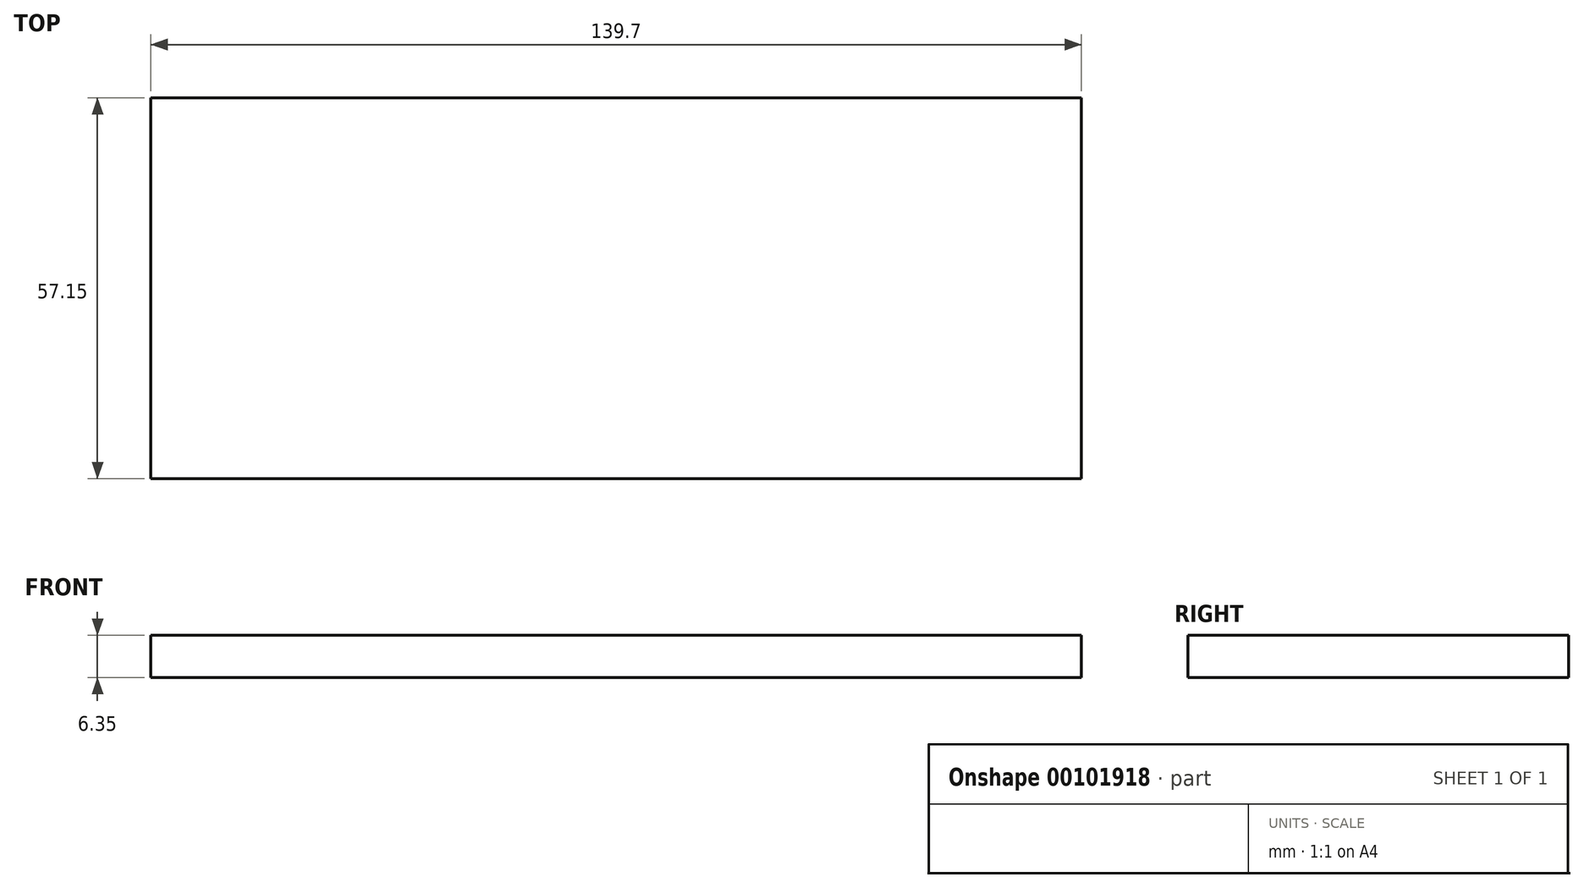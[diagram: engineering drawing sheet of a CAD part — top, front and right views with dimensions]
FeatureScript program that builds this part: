
annotation { "Feature Type Name" : "Feature", "Feature Type Description" : "" }
export const myFeature = defineFeature(function(context is Context, id is Id, definition is map)
    precondition{}
    {
        {
            var Q0;
            Q0=qCreatedBy(makeId("Top.planeOp"),FACE);
            var sketch = newSketch(context, id + "F0", { "sketchPlane" : qUnion([Q0])});
            skLineSegment(sketch, "E0.bottom", {"start": v(0, 0) * mm, "end": v(139.7, 0) * mm});
            skLineSegment(sketch, "E0.top", {"start": v(0, 57.15) * mm, "end": v(139.7, 57.15) * mm});
            skLineSegment(sketch, "E0.left", {"start": v(0, 0) * mm, "end": v(0, 57.15) * mm});
            skLineSegment(sketch, "E0.right", {"start": v(139.7, 0) * mm, "end": v(139.7, 57.15) * mm});
            skSolve(sketch);
        }
        {
            var Q0;
            Q0=makeQuery(id+"F0.imprint","IMPRINT",FACE,{"disambiguationData":[TD([[makeQuery(id+"F0.imprint","IMPRINT",EDGE,{"derivedFrom":sQuery(id+"F0.wireOp",EDGE,"E0.bottom")}),1.0]])]});
            extrude(context, id + "F1", {"entities" : qUnion([Q0]), "depth" : 6.35 * mm});
        }
    });
